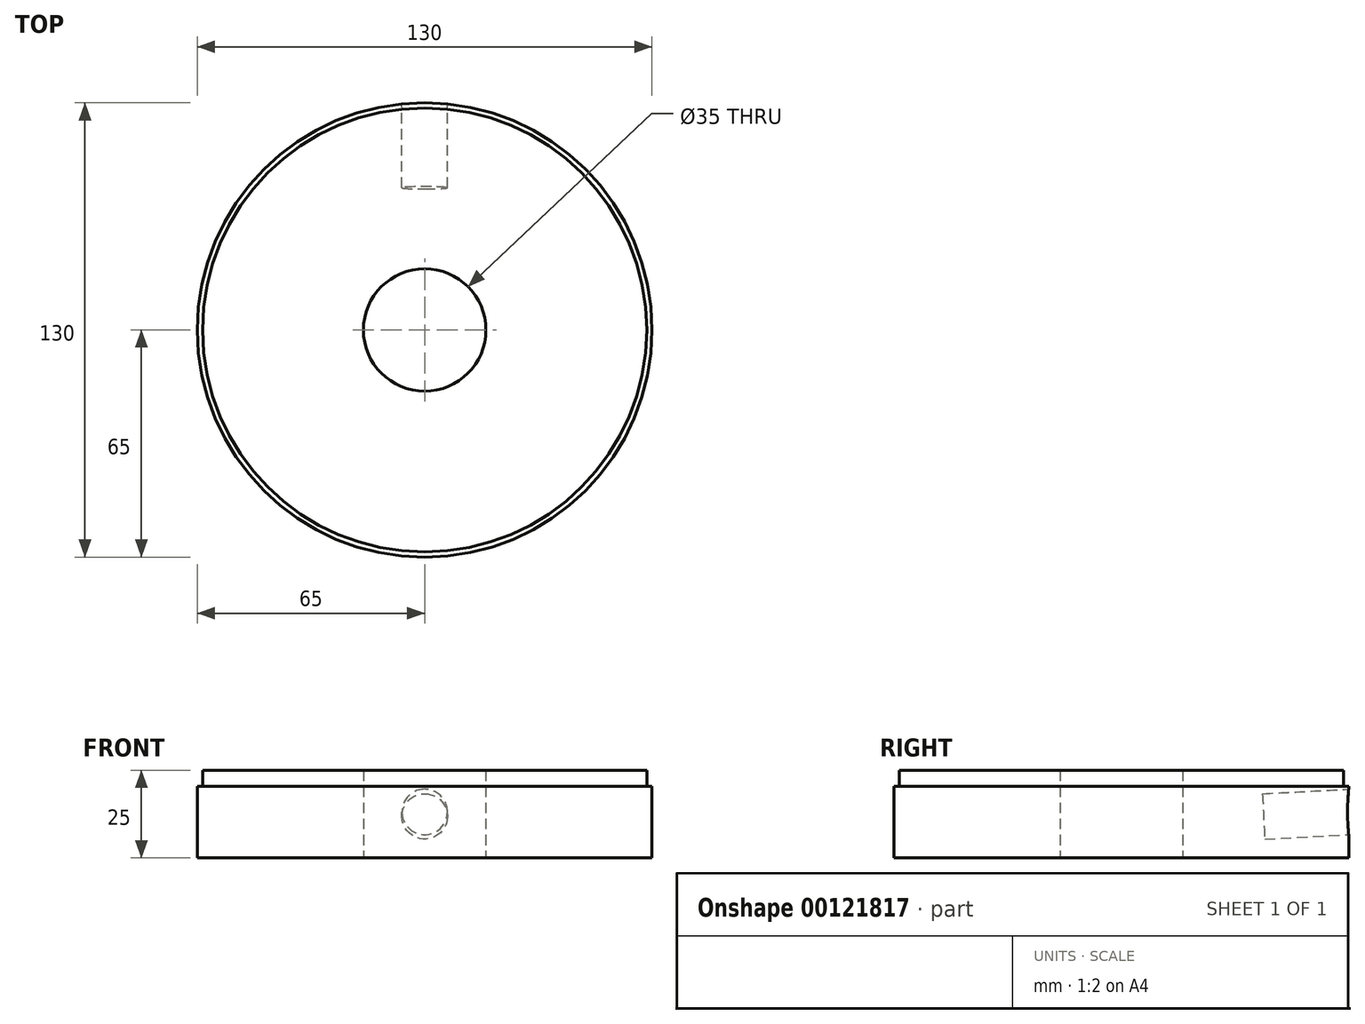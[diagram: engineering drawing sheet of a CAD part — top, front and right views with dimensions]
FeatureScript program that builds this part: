
annotation { "Feature Type Name" : "Feature", "Feature Type Description" : "" }
export const myFeature = defineFeature(function(context is Context, id is Id, definition is map)
    precondition{}
    {
        {
            var Q0;
            Q0=qCreatedBy(makeId("Top.planeOp"),FACE);
            var sketch = newSketch(context, id + "F0", { "sketchPlane" : qUnion([Q0])});
            skCircle(sketch, "E0", {"center": v(0, 0) * mm, "radius": 65 * mm});
            skCircle(sketch, "E1", {"center": v(0, 0) * mm, "radius": 17.5 * mm});
            skSolve(sketch);
        }
        {
            var Q0;
            Q0 = qSketchRegion(id + "F0", true);
            extrude(context, id + "F1", {"entities" : qUnion([Q0]), "depth" : 25 * mm});
        }
        {
            var Q0;
            Q0=makeQuery(id+"F1.opExtrude","CAP_FACE",FACE,{"disambiguationData":[OSD([sQuery(id+"F0.wireOp",EDGE,"E0"),sQuery(id+"F0.wireOp",EDGE,"E1")])],"isStart":false});
            var sketch = newSketch(context, id + "F2", { "sketchPlane" : qUnion([Q0])});
            skLineSegment(sketch, "E2", {"start": v(0, 0) * mm, "end": v(0, 78.95) * mm});
            skLineSegment(sketch, "E3", {"start": v(0, 78.95) * mm, "end": v(0, -79.41) * mm});
            skLineSegment(sketch, "E4", {"start": v(79.62, 0) * mm, "end": v(-84.7, 0) * mm});
            skLineSegment(sketch, "E5", {"start": v(0, 0) * mm, "end": v(-64.13, 68.26) * mm});
            skLineSegment(sketch, "E6", {"start": v(-64.13, 68.26) * mm, "end": v(0, 0) * mm});
            skLineSegment(sketch, "E7", {"start": v(0, 0) * mm, "end": v(63.23, -67.31) * mm});
            skLineSegment(sketch, "E8", {"start": v(0, 0) * mm, "end": v(56.09, 52.69) * mm});
            skLineSegment(sketch, "E9", {"start": v(0, 0) * mm, "end": v(-60.4, -56.74) * mm});
            skSolve(sketch);
        }
        {
            var Q0;
            Q0=qCreatedBy(makeId("Front.planeOp"),FACE);
            cPlane(context, id + "F3", {"entities" : qUnion([Q0]), "cplaneType" : CPlaneType.OFFSET, "offset" : 65 * mm, "oppositeDirection" : true, "width" : 150 * mm, "height" : 150 * mm});
        }
        {
            var Q0;
            Q0=qCreatedBy(makeId("Top.planeOp"),FACE);
            var sketch = newSketch(context, id + "F4", { "sketchPlane" : qUnion([Q0])});
            skLineSegment(sketch, "E10", {"start": v(0, 0) * mm, "end": v(56.09, 52.7) * mm});
            skLineSegment(sketch, "E11", {"start": v(56.09, 52.7) * mm, "end": v(-60.4, -56.74) * mm});
            skLineSegment(sketch, "E12", {"start": v(63.24, -67.32) * mm, "end": v(-64.13, 68.26) * mm});
            skSolve(sketch);
        }
        {
            var Q0;
            Q0=qCreatedBy(makeId("Right.planeOp"),FACE);
            var sketch = newSketch(context, id + "F5", { "sketchPlane" : qUnion([Q0])});
            skLineSegment(sketch, "E13", {"start": v(65.02, 25) * mm, "end": v(65.02, -3.95) * mm});
            skLineSegment(sketch, "E14", {"start": v(65.02, 25) * mm, "end": v(66.47, -2.69) * mm});
            skSolve(sketch);
        }
        {
            var Q0;
            Q0=qCreatedBy(id+"F3.planeOp",FACE);
            var sketch = newSketch(context, id + "F6", { "sketchPlane" : qUnion([Q0])});
            skLineSegment(sketch, "E15", {"start": v(0, 25.25) * mm, "end": v(-71.22, 25.25) * mm});
            skSolve(sketch);
        }
        {
            var Q0;
            Q0=sQuery(id+"F5.wireOp",VERTEX,"E14.end");
            var Q1;
            Q1=sQuery(id+"F6.wireOp",VERTEX,"E15.start");
            var Q2;
            Q2=sQuery(id+"F6.wireOp",VERTEX,"E15.end");
            cPlane(context, id + "F7", {"entities" : qUnion([Q0, Q1, Q2]), "cplaneType" : CPlaneType.THREE_POINT, "offset" : 25 * mm, "width" : 150 * mm, "height" : 150 * mm});
        }
        {
            var Q0;
            Q0=qCreatedBy(id+"F7.planeOp",FACE);
            var sketch = newSketch(context, id + "F8", { "sketchPlane" : qUnion([Q0])});
            skLineSegment(sketch, "E16", {"start": v(0, -3.32) * mm, "end": v(0, 9.68) * mm});
            skCircle(sketch, "E17", {"center": v(0, 9.68) * mm, "radius": 6.5 * mm});
            skSolve(sketch);
        }
        {
            var Q0;
            Q0=makeQuery(id+"F8.imprint","IMPRINT",FACE,{"disambiguationData":[TD([[makeQuery(id+"F8.imprint","IMPRINT",EDGE,{"derivedFrom":sQuery(id+"F8.wireOp",EDGE,"E17")}),1.0]])]});
            extrude(context, id + "F9", {"entities" : qUnion([Q0]), "operationType" : NewBodyOperationType.REMOVE, "oppositeDirection" : true, "depth" : 25 * mm});
        }
        {
            var Q0;
            Q0=makeQuery(id+"F1.opExtrude","CAP_FACE",FACE,{"disambiguationData":[OSD([sQuery(id+"F0.wireOp",EDGE,"E0"),sQuery(id+"F0.wireOp",EDGE,"E1")])],"isStart":false});
            var sketch = newSketch(context, id + "F10", { "sketchPlane" : qUnion([Q0])});
            skCircle(sketch, "E18", {"center": v(0, 0) * mm, "radius": 63.5 * mm});
            skCircle(sketch, "E19", {"center": v(0, 0) * mm, "radius": 65 * mm});
            skSolve(sketch);
        }
        {
            var Q0;
            Q0 = qSketchRegion(id + "F10", true);
            extrude(context, id + "F11", {"entities" : qUnion([Q0]), "operationType" : NewBodyOperationType.REMOVE, "oppositeDirection" : true, "depth" : 4.5 * mm});
        }
    });
